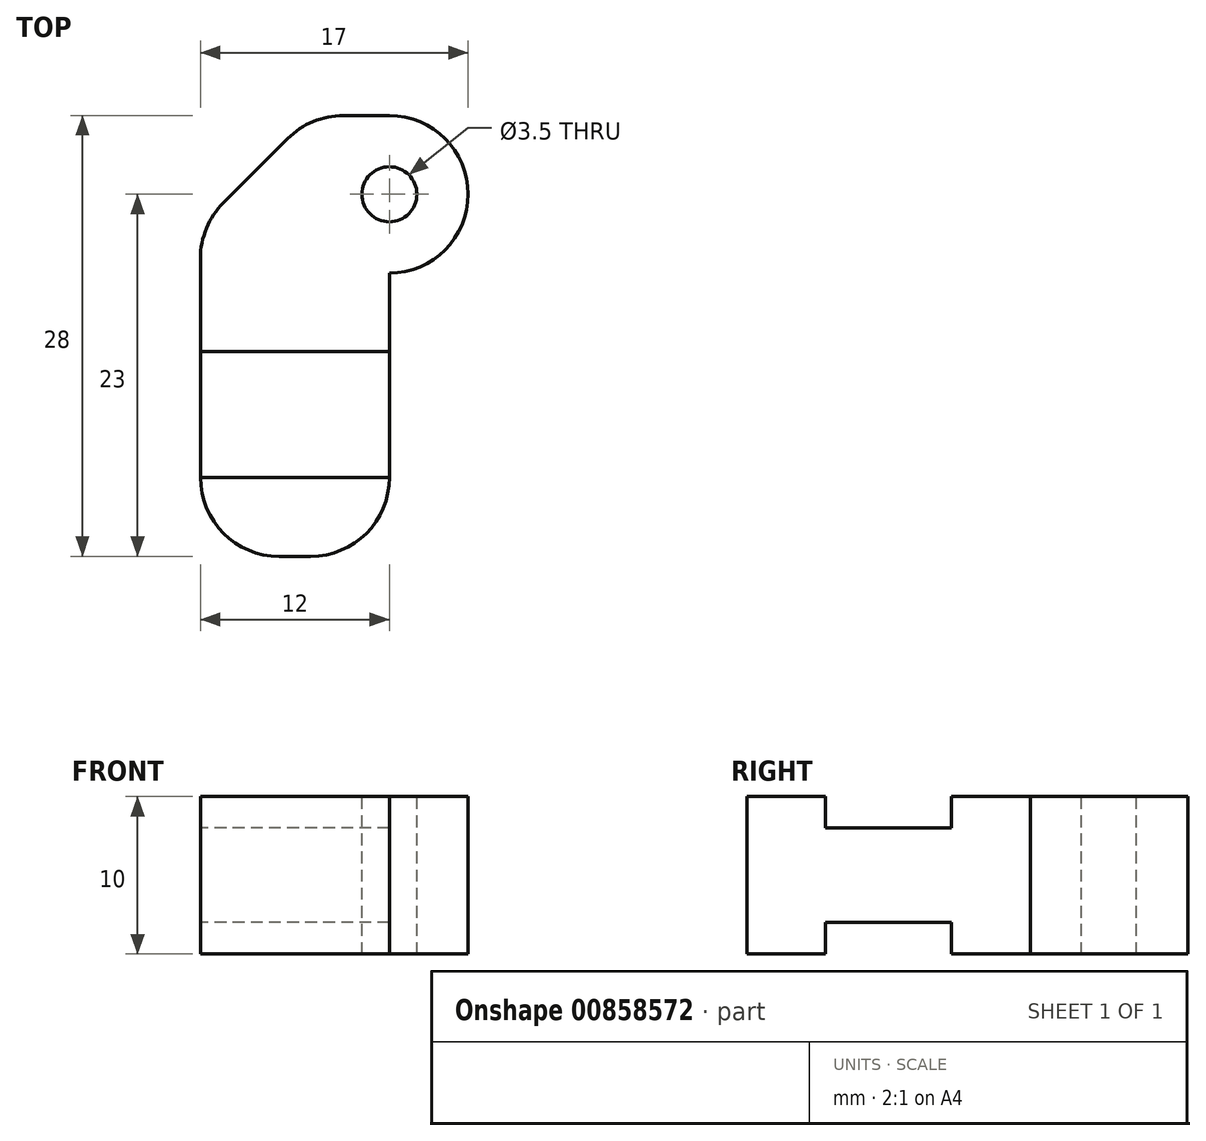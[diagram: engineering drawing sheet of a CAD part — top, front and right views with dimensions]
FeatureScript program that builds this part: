
annotation { "Feature Type Name" : "Feature", "Feature Type Description" : "" }
export const myFeature = defineFeature(function(context is Context, id is Id, definition is map)
    precondition{}
    {
        {
            var Q0;
            Q0=qCreatedBy(makeId("Top.planeOp"),FACE);
            var sketch = newSketch(context, id + "F0", { "sketchPlane" : qUnion([Q0])});
            skLineSegment(sketch, "E0.bottom", {"start": v(0, 0) * mm, "end": v(12, 0) * mm});
            skLineSegment(sketch, "E0.top", {"start": v(0, -28) * mm, "end": v(12, -28) * mm});
            skLineSegment(sketch, "E0.left", {"start": v(0, 0) * mm, "end": v(0, -28) * mm});
            skLineSegment(sketch, "E0.right", {"start": v(12, 0) * mm, "end": v(12, -28) * mm});
            skLineSegment(sketch, "E1.bottom", {"start": v(12, 0) * mm, "end": v(17, 0) * mm});
            skLineSegment(sketch, "E1.top", {"start": v(12, -10) * mm, "end": v(17, -10) * mm});
            skLineSegment(sketch, "E1.left", {"start": v(12, 0) * mm, "end": v(12, -10) * mm});
            skLineSegment(sketch, "E1.right", {"start": v(17, 0) * mm, "end": v(17, -10) * mm});
            skSolve(sketch);
        }
        {
            var Q0;
            {var subQ0=sQuery(id+"F0.wireOp",EDGE,"E1.bottom");var subQ2=sQuery(id+"F0.wireOp",EDGE,"E0.bottom");Q0=qUnion([makeQuery(id+"F0.imprint","IMPRINT",FACE,{"disambiguationData":[TD([[makeQuery(id+"F0.imprint","IMPRINT",EDGE,{"derivedFrom":subQ2}),-1.0]])]}),makeQuery(id+"F0.imprint","IMPRINT",FACE,{"disambiguationData":[TD([[makeQuery(id+"F0.imprint","IMPRINT",EDGE,{"derivedFrom":subQ0}),-1.0]])]})]);}
            extrude(context, id + "F1", {"entities" : qUnion([Q0]), "depth" : 10 * mm, "offsetDistance" : 25 * mm});
        }
        {
            var Q0;
            Q0=makeQuery(id+"F1.opExtrude","CAP_FACE",FACE,{"disambiguationData":[OSD([sQuery(id+"F0.wireOp",EDGE,"E0.bottom"),sQuery(id+"F0.wireOp",EDGE,"E0.top"),sQuery(id+"F0.wireOp",EDGE,"E0.left"),sQuery(id+"F0.wireOp",EDGE,"E0.right"),sQuery(id+"F0.wireOp",EDGE,"E1.bottom"),sQuery(id+"F0.wireOp",EDGE,"E1.top"),sQuery(id+"F0.wireOp",EDGE,"E1.right")])],"isStart":false});
            var sketch = newSketch(context, id + "F2", { "sketchPlane" : qUnion([Q0])});
            skLineSegment(sketch, "E2", {"start": v(17, -5) * mm, "end": v(12, -5) * mm});
            skCircle(sketch, "E3", {"center": v(12, -5) * mm, "radius": 1.75 * mm});
            skSolve(sketch);
        }
        {
            var Q0;
            Q0 = qSketchRegion(id + "F2", true);
            extrude(context, id + "F3", {"entities" : qUnion([Q0]), "operationType" : NewBodyOperationType.REMOVE, "oppositeDirection" : true, "depth" : 25 * mm, "offsetDistance" : 25 * mm});
        }
        {
            var Q0;
            Q0=makeQuery(id+"F1.opExtrude","SWEPT_FACE",FACE,{"disambiguationData":[OSD([sQuery(id+"F0.wireOp",EDGE,"E0.left")])]});
            var sketch = newSketch(context, id + "F4", { "sketchPlane" : qUnion([Q0])});
            skLineSegment(sketch, "E4", {"start": v(28, 0) * mm, "end": v(23, 0) * mm});
            skLineSegment(sketch, "E5.bottom", {"start": v(23, 0) * mm, "end": v(15, 0) * mm});
            skLineSegment(sketch, "E5.top", {"start": v(23, 2) * mm, "end": v(15, 2) * mm});
            skLineSegment(sketch, "E5.left", {"start": v(23, 0) * mm, "end": v(23, 2) * mm});
            skLineSegment(sketch, "E5.right", {"start": v(15, 0) * mm, "end": v(15, 2) * mm});
            skLineSegment(sketch, "E6", {"start": v(28, 10) * mm, "end": v(23, 10) * mm});
            skLineSegment(sketch, "E7.bottom", {"start": v(23, 10) * mm, "end": v(15, 10) * mm});
            skLineSegment(sketch, "E7.top", {"start": v(23, 8) * mm, "end": v(15, 8) * mm});
            skLineSegment(sketch, "E7.left", {"start": v(23, 10) * mm, "end": v(23, 8) * mm});
            skLineSegment(sketch, "E7.right", {"start": v(15, 10) * mm, "end": v(15, 8) * mm});
            skSolve(sketch);
        }
        {
            var Q0;
            Q0 = qSketchRegion(id + "F4", true);
            extrude(context, id + "F5", {"entities" : qUnion([Q0]), "operationType" : NewBodyOperationType.REMOVE, "oppositeDirection" : true, "depth" : 25 * mm, "offsetDistance" : 25 * mm});
        }
        {
            var Q0;
            Q0=makeQuery(id+"F1.opExtrude","SWEPT_EDGE",EDGE,{"disambiguationData":[OSD([sQuery(id+"F0.wireOp",EDGE,"E0.top"),sQuery(id+"F0.wireOp",EDGE,"E0.right")])]});
            var Q1;
            Q1=makeQuery(id+"F1.opExtrude","SWEPT_EDGE",EDGE,{"disambiguationData":[OSD([sQuery(id+"F0.wireOp",EDGE,"E0.top"),sQuery(id+"F0.wireOp",EDGE,"E0.left")])]});
            var Q2;
            Q2=makeQuery(id+"F1.opExtrude","SWEPT_EDGE",EDGE,{"disambiguationData":[OSD([sQuery(id+"F0.wireOp",EDGE,"E1.bottom"),sQuery(id+"F0.wireOp",EDGE,"E1.right")])]});
            var Q3;
            Q3=makeQuery(id+"F1.opExtrude","SWEPT_EDGE",EDGE,{"disambiguationData":[OSD([sQuery(id+"F0.wireOp",EDGE,"E1.top"),sQuery(id+"F0.wireOp",EDGE,"E1.right")])]});
            fillet(context, id + "F6", {"entities" : qUnion([Q0, Q1, Q2, Q3]), "radius" : 5 * mm, "tangentPropagation" : true, "allowEdgeOverflow" : false});
        }
        {
            var Q0;
            Q0=makeQuery(id+"F1.opExtrude","SWEPT_EDGE",EDGE,{"disambiguationData":[OSD([sQuery(id+"F0.wireOp",EDGE,"E0.bottom"),sQuery(id+"F0.wireOp",EDGE,"E0.left")])]});
            chamfer(context, id + "F7", {"entities" : qUnion([Q0]), "width" : 7 * mm, "tangentPropagation" : true});
        }
        {
            var Q0;
            {var subQ0=sQuery(id+"F0.wireOp",EDGE,"E0.bottom");Q0=makeQuery(id+"F7.opChamfer","BLEND_EDGE",EDGE,{"blendedFrom":[makeQuery(id+"F1.opExtrude","SWEPT_EDGE",EDGE,{"disambiguationData":[OSD([subQ0,sQuery(id+"F0.wireOp",EDGE,"E0.left")])]}),makeQuery(id+"F1.opExtrude","SWEPT_FACE",FACE,{"disambiguationData":[OSD([subQ0,sQuery(id+"F0.wireOp",EDGE,"E1.bottom")])]})],"blendedInto":[makeQuery(id+"F1.opExtrude","SWEPT_FACE",FACE,{"disambiguationData":[OSD([subQ0,sQuery(id+"F0.wireOp",EDGE,"E1.bottom")])]})]});}
            var Q1;
            {var subQ0=sQuery(id+"F0.wireOp",EDGE,"E0.left");Q1=makeQuery(id+"F7.opChamfer","BLEND_EDGE",EDGE,{"blendedFrom":[makeQuery(id+"F1.opExtrude","SWEPT_EDGE",EDGE,{"disambiguationData":[OSD([sQuery(id+"F0.wireOp",EDGE,"E0.bottom"),subQ0])]}),makeQuery(id+"F1.opExtrude","SWEPT_FACE",FACE,{"disambiguationData":[OSD([subQ0])]})],"blendedInto":[makeQuery(id+"F1.opExtrude","SWEPT_FACE",FACE,{"disambiguationData":[OSD([subQ0])]})]});}
            fillet(context, id + "F8", {"entities" : qUnion([Q0, Q1]), "radius" : 5 * mm, "tangentPropagation" : true, "allowEdgeOverflow" : false});
        }
    });
